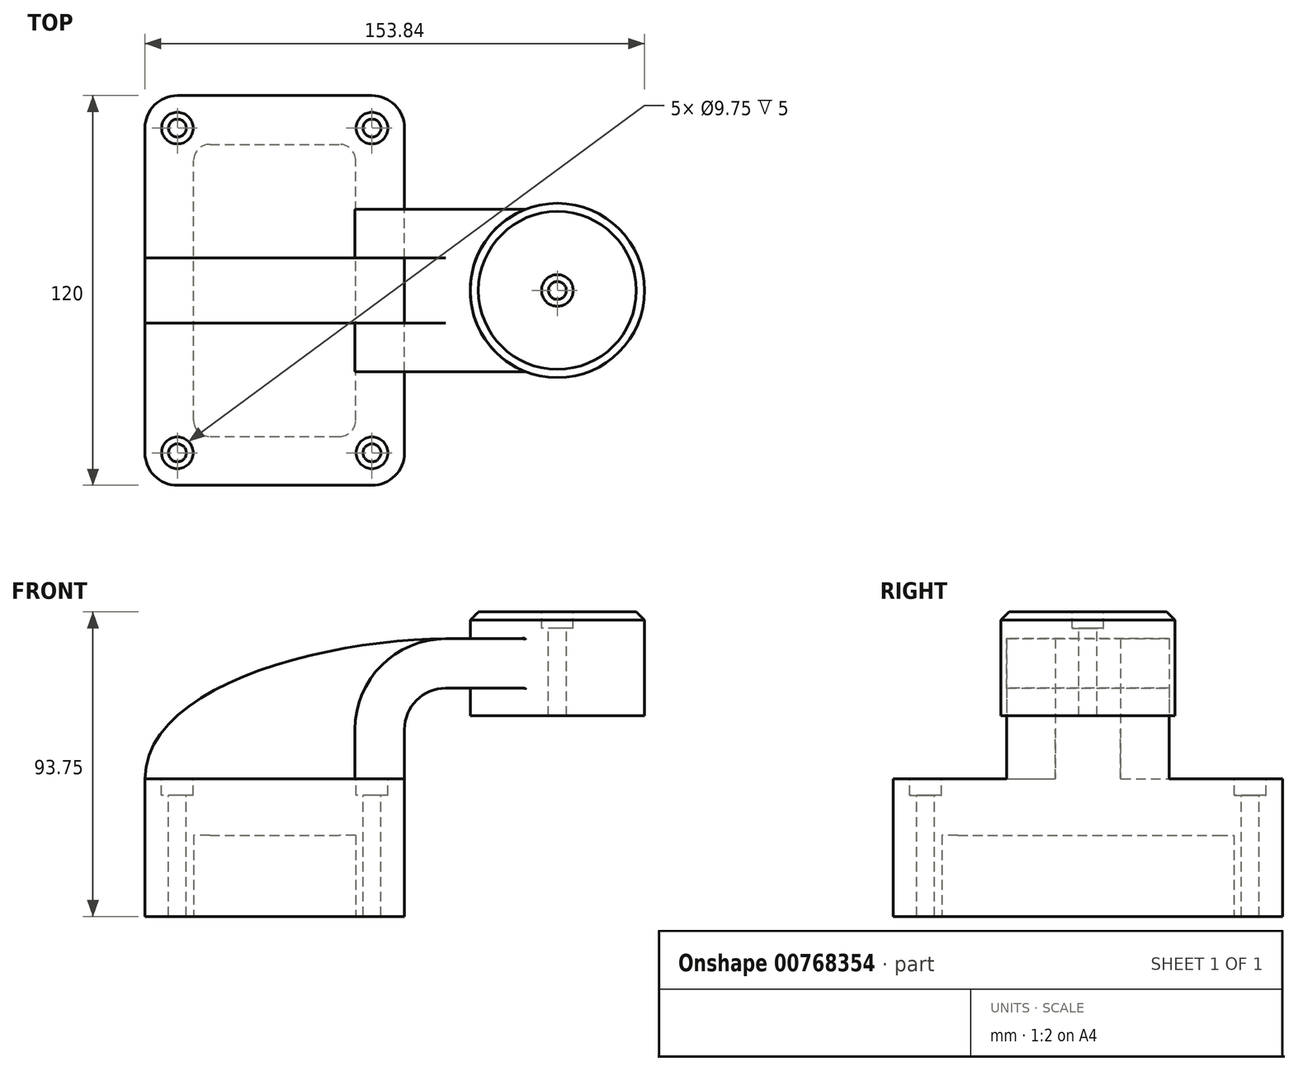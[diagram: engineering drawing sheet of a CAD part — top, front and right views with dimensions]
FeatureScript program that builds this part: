
annotation { "Feature Type Name" : "Feature", "Feature Type Description" : "" }
export const myFeature = defineFeature(function(context is Context, id is Id, definition is map)
    precondition{}
    {
        {
            assignVariable(context, id + "F0", {"name" : "chamferRadius", "anyValue" : 0.2});
        }
        {
            var Q0;
            Q0=qCreatedBy(makeId("Front.planeOp"),FACE);
            var sketch = newSketch(context, id + "F1", { "sketchPlane" : qUnion([Q0])});
            skLineSegment(sketch, "E0.bottom", {"start": v(39.95, -21.16) * mm, "end": v(-39.95, -21.16) * mm});
            skLineSegment(sketch, "E0.top", {"start": v(39.95, 21.16) * mm, "end": v(-39.95, 21.16) * mm});
            skLineSegment(sketch, "E0.left", {"start": v(39.95, -21.16) * mm, "end": v(39.95, 21.16) * mm});
            skLineSegment(sketch, "E0.right", {"start": v(-39.95, -21.16) * mm, "end": v(-39.95, 21.16) * mm});
            skPoint(sketch, "E0.middle", {"position": v(0, 0) * mm});
            skLineSegment(sketch, "E1.bottom", {"start": v(113.89, 40.6) * mm, "end": v(60.19, 40.6) * mm});
            skLineSegment(sketch, "E1.top", {"start": v(113.89, 72.6) * mm, "end": v(60.19, 72.6) * mm});
            skLineSegment(sketch, "E1.left", {"start": v(113.89, 40.6) * mm, "end": v(113.89, 72.6) * mm});
            skLineSegment(sketch, "E1.right", {"start": v(60.19, 40.6) * mm, "end": v(60.19, 72.6) * mm});
            skPoint(sketch, "E1.middle", {"position": v(87.04, 56.6) * mm});
            skLineSegment(sketch, "E2", {"start": v(39.95, 21.16) * mm, "end": v(39.95, 36.4) * mm});
            skArc(sketch, "E3", {"start": v(52.65, 49.1) * mm, "mid": v(43.67, 45.38) * mm, "end": v(39.95, 36.4) * mm});
            skLineSegment(sketch, "E4", {"start": v(52.65, 49.1) * mm, "end": v(87.04, 49.1) * mm});
            skLineSegment(sketch, "E5.0", {"start": v(24.71, 21.16) * mm, "end": v(24.71, 36.4) * mm});
            skArc(sketch, "E5.1", {"start": v(52.65, 64.34) * mm, "mid": v(32.9, 56.16) * mm, "end": v(24.71, 36.4) * mm});
            skLineSegment(sketch, "E5.2", {"start": v(52.65, 64.34) * mm, "end": v(87.04, 64.34) * mm});
            skLineSegment(sketch, "E6", {"start": v(87.04, 72.6) * mm, "end": v(87.04, 40.6) * mm});
            skFitSpline(sketch, "E7", {"points": [v(52.65, 64.34) * mm, v(-39.95, 21.16) * mm], "startDerivative": vector(-108.23, 0) * mm, "endDerivative": vector(0, -87.13) * mm});
            skSolve(sketch);
        }
        {
            var Q0;
            Q0=makeQuery(id+"F1.imprint","IMPRINT",FACE,{"disambiguationData":[TD([[makeQuery(id+"F1.imprint","IMPRINT",EDGE,{"derivedFrom":sQuery(id+"F1.wireOp",EDGE,"E0.bottom")}),-1.0]])]});
            extrude(context, id + "F2", {"entities" : qUnion([Q0]), "endBound" : BoundingType.SYMMETRIC, "depth" : 120 * mm, "offsetDistance" : 25.4 * mm});
        }
        {
            var Q0;
            {var subQ1=sQuery(id+"F1.wireOp",EDGE,"E2");Q0=makeQuery(id+"F1.imprint","IMPRINT",FACE,{"disambiguationData":[TD([[makeQuery(id+"F1.imprint","IMPRINT",EDGE,{"derivedFrom":subQ1}),1.0]])]});}
            var Q1;
            {var subQ0=sQuery(id+"F1.wireOp",EDGE,"E4");var subQ1=sQuery(id+"F1.wireOp",EDGE,"E1.right");var subQ2=makeQuery(id+"F1.imprint","INTERSECT",VERTEX,{"derivedFrom":[subQ1,subQ0]});Q1=makeQuery(id+"F1.imprint","IMPRINT",FACE,{"disambiguationData":[TD([[makeQuery(id+"F1.imprint","IMPRINT",EDGE,{"disambiguationData":[TD([[subQ2,-1.0]])],"derivedFrom":subQ1}),-1.0]])]});}
            extrude(context, id + "F3", {"entities" : qUnion([Q0, Q1]), "operationType" : NewBodyOperationType.ADD, "endBound" : BoundingType.SYMMETRIC, "depth" : 50 * mm, "offsetDistance" : 25.4 * mm});
        }
        {
            var Q0;
            {var subQ2=sQuery(id+"F1.wireOp",EDGE,"E5.0");Q0=makeQuery(id+"F1.imprint","IMPRINT",FACE,{"disambiguationData":[TD([[makeQuery(id+"F1.imprint","IMPRINT",EDGE,{"derivedFrom":subQ2}),1.0]])]});}
            extrude(context, id + "F4", {"entities" : qUnion([Q0]), "operationType" : NewBodyOperationType.ADD, "endBound" : BoundingType.SYMMETRIC, "depth" : 20 * mm, "offsetDistance" : 25.4 * mm});
        }
        {
            var Q0;
            {var subQ4=sQuery(id+"F1.wireOp",EDGE,"E1.left");Q0=makeQuery(id+"F1.imprint","IMPRINT",FACE,{"disambiguationData":[TD([[makeQuery(id+"F1.imprint","IMPRINT",EDGE,{"derivedFrom":subQ4}),1.0]])]});}
            var Q1;
            Q1=sQuery(id+"F1.wireOp",EDGE,"E6");
            revolve(context, id + "F5", {"operationType" : NewBodyOperationType.ADD, "surfaceOperationType" : NewSurfaceOperationType.NEW, "entities" : qUnion([Q0]), "axis" : qUnion([Q1]), "revolveType" : RevolveType.FULL});
        }
        {
            var Q0;
            Q0=makeQuery(id+"F2.opExtrude","CAP_EDGE",EDGE,{"disambiguationData":[OSD([sQuery(id+"F1.wireOp",EDGE,"E0.left")])],"isStart":false});
            var Q1;
            Q1=makeQuery(id+"F2.opExtrude","CAP_EDGE",EDGE,{"disambiguationData":[OSD([sQuery(id+"F1.wireOp",EDGE,"E0.right")])],"isStart":false});
            var Q2;
            Q2=makeQuery(id+"F2.opExtrude","CAP_EDGE",EDGE,{"disambiguationData":[OSD([sQuery(id+"F1.wireOp",EDGE,"E0.left")])],"isStart":true});
            var Q3;
            Q3=makeQuery(id+"F2.opExtrude","CAP_EDGE",EDGE,{"disambiguationData":[OSD([sQuery(id+"F1.wireOp",EDGE,"E0.right")])],"isStart":true});
            fillet(context, id + "F6", {"entities" : qUnion([Q0, Q1, Q2, Q3]), "radius" : 10 * mm, "tangentPropagation" : true, "allowEdgeOverflow" : false});
        }
        {
            var Q0;
            Q0=makeQuery(id+"F5.boolean.opBoolean","INTERSECT",EDGE,{"derivedFrom":[makeQuery(id+"F3.opExtrude","CAP_FACE",FACE,{"disambiguationData":[OSD([sQuery(id+"F1.wireOp",EDGE,"E0.top"),sQuery(id+"F1.wireOp",EDGE,"E2"),sQuery(id+"F1.wireOp",EDGE,"E3"),sQuery(id+"F1.wireOp",EDGE,"E4"),sQuery(id+"F1.wireOp",EDGE,"E5.0"),sQuery(id+"F1.wireOp",EDGE,"E5.1"),sQuery(id+"F1.wireOp",EDGE,"E5.2"),sQuery(id+"F1.wireOp",EDGE,"E6")])],"isStart":true}),makeQuery(id+"F5.opRevolve","SWEPT_FACE",FACE,{"disambiguationData":[OSD([sQuery(id+"F1.wireOp",EDGE,"E1.left")])]})]});
            var Q1;
            Q1=makeQuery(id+"F5.boolean.opBoolean","INTERSECT",EDGE,{"derivedFrom":[makeQuery(id+"F3.opExtrude","SWEPT_FACE",FACE,{"disambiguationData":[OSD([sQuery(id+"F1.wireOp",EDGE,"E5.2")])]}),makeQuery(id+"F5.opRevolve","SWEPT_FACE",FACE,{"disambiguationData":[OSD([sQuery(id+"F1.wireOp",EDGE,"E1.left")])]})]});
            var Q2;
            Q2=makeQuery(id+"F5.boolean.opBoolean","INTERSECT",EDGE,{"derivedFrom":[makeQuery(id+"F3.opExtrude","CAP_FACE",FACE,{"disambiguationData":[OSD([sQuery(id+"F1.wireOp",EDGE,"E0.top"),sQuery(id+"F1.wireOp",EDGE,"E2"),sQuery(id+"F1.wireOp",EDGE,"E3"),sQuery(id+"F1.wireOp",EDGE,"E4"),sQuery(id+"F1.wireOp",EDGE,"E5.0"),sQuery(id+"F1.wireOp",EDGE,"E5.1"),sQuery(id+"F1.wireOp",EDGE,"E5.2"),sQuery(id+"F1.wireOp",EDGE,"E6")])],"isStart":false}),makeQuery(id+"F5.opRevolve","SWEPT_FACE",FACE,{"disambiguationData":[OSD([sQuery(id+"F1.wireOp",EDGE,"E1.left")])]})]});
            var Q3;
            Q3=makeQuery(id+"F5.boolean.opBoolean","INTERSECT",EDGE,{"derivedFrom":[makeQuery(id+"F3.opExtrude","SWEPT_FACE",FACE,{"disambiguationData":[OSD([sQuery(id+"F1.wireOp",EDGE,"E4")])]}),makeQuery(id+"F5.opRevolve","SWEPT_FACE",FACE,{"disambiguationData":[OSD([sQuery(id+"F1.wireOp",EDGE,"E1.left")])]})]});
            var Q4;
            Q4=makeQuery(id+"F3.opExtrude","CAP_EDGE",EDGE,{"disambiguationData":[OSD([sQuery(id+"F1.wireOp",EDGE,"E5.2")])],"isStart":false});
            var Q5;
            Q5=makeQuery(id+"F3.opExtrude","CAP_EDGE",EDGE,{"disambiguationData":[OSD([sQuery(id+"F1.wireOp",EDGE,"E5.2")])],"isStart":true});
            var Q6;
            Q6=makeQuery(id+"F3.opExtrude","CAP_EDGE",EDGE,{"disambiguationData":[OSD([sQuery(id+"F1.wireOp",EDGE,"E5.1")])],"isStart":false});
            var Q7;
            Q7=makeQuery(id+"F3.opExtrude","CAP_EDGE",EDGE,{"disambiguationData":[OSD([sQuery(id+"F1.wireOp",EDGE,"E5.0")])],"isStart":false});
            var Q8;
            Q8=makeQuery(id+"F3.opExtrude","CAP_EDGE",EDGE,{"disambiguationData":[OSD([sQuery(id+"F1.wireOp",EDGE,"E5.1")])],"isStart":true});
            var Q9;
            Q9=makeQuery(id+"F3.opExtrude","CAP_EDGE",EDGE,{"disambiguationData":[OSD([sQuery(id+"F1.wireOp",EDGE,"E5.0")])],"isStart":true});
            var Q10;
            Q10=makeQuery(id+"F3.opExtrude","CAP_EDGE",EDGE,{"disambiguationData":[OSD([sQuery(id+"F1.wireOp",EDGE,"E0.top")])],"isStart":true});
            var Q11;
            {var subQ0=sQuery(id+"F1.wireOp",EDGE,"E0.top");var subQ1=sQuery(id+"F1.wireOp",EDGE,"E5.1");var subQ2=sQuery(id+"F1.wireOp",EDGE,"E5.0");Q11=makeQuery(id+"F4.boolean.opBoolean","SPLIT",EDGE,{"disambiguationData":[TD([makeQuery(id+"F4.opExtrude","CAP_FACE",FACE,{"disambiguationData":[OSD([subQ0,subQ2,subQ1,sQuery(id+"F1.wireOp",EDGE,"E7")])],"isStart":true})])],"derivedFrom":makeQuery(id+"F3.opExtrude","SWEPT_EDGE",EDGE,{"disambiguationData":[OSD([subQ0,subQ2])]})});}
            var Q12;
            {var subQ0=sQuery(id+"F1.wireOp",EDGE,"E0.top");var subQ1=sQuery(id+"F1.wireOp",EDGE,"E5.1");var subQ2=sQuery(id+"F1.wireOp",EDGE,"E5.0");Q12=makeQuery(id+"F4.boolean.opBoolean","SPLIT",EDGE,{"disambiguationData":[TD([makeQuery(id+"F4.opExtrude","CAP_FACE",FACE,{"disambiguationData":[OSD([subQ0,subQ2,subQ1,sQuery(id+"F1.wireOp",EDGE,"E7")])],"isStart":false})])],"derivedFrom":makeQuery(id+"F3.opExtrude","SWEPT_EDGE",EDGE,{"disambiguationData":[OSD([subQ0,subQ2])]})});}
            var Q13;
            Q13=makeQuery(id+"F3.opExtrude","CAP_EDGE",EDGE,{"disambiguationData":[OSD([sQuery(id+"F1.wireOp",EDGE,"E0.top")])],"isStart":false});
            var Q14;
            Q14=makeQuery(id+"F4.opExtrude","CAP_EDGE",EDGE,{"disambiguationData":[OSD([sQuery(id+"F1.wireOp",EDGE,"E0.top")])],"isStart":true});
            var Q15;
            Q15=makeQuery(id+"F4.opExtrude","CAP_EDGE",EDGE,{"disambiguationData":[OSD([sQuery(id+"F1.wireOp",EDGE,"E0.top")])],"isStart":false});
            fillet(context, id + "F7", {"entities" : qUnion([Q0, Q1, Q2, Q3, Q4, Q5, Q6, Q7, Q8, Q9, Q10, Q11, Q12, Q13, Q14, Q15]), "radius" : (getVariable(context, 'chamferRadius')) * mm, "tangentPropagation" : true, "allowEdgeOverflow" : false});
        }
        {
            var Q0;
            Q0=makeQuery(id+"F5.opRevolve","SWEPT_FACE",FACE,{"disambiguationData":[OSD([sQuery(id+"F1.wireOp",EDGE,"E1.top")])]});
            var sketch = newSketch(context, id + "F8", { "sketchPlane" : qUnion([Q0])});
            skPoint(sketch, "E8", {"position": v(87.04, 0) * mm});
            skSolve(sketch);
        }
        {
            var Q0;
            Q0=sQuery(id+"F8.wireOp",VERTEX,"E8");
            var Q1;
            Q1=makeQuery(id+"F2.opExtrude","SWEPT_BODY",BODY,{"disambiguationData":[OSD([sQuery(id+"F1.wireOp",EDGE,"E0.bottom"),sQuery(id+"F1.wireOp",EDGE,"E0.top"),sQuery(id+"F1.wireOp",EDGE,"E0.left"),sQuery(id+"F1.wireOp",EDGE,"E0.right")])]});
            hole(context, id + "F9", {"style" : HoleStyle.C_BORE, "endStyle" : HoleEndStyle.THROUGH, "standardTappedOrClearance" : lookupTablePath({ "standard" : "ISO", "fit" : "Normal", "engagement" : "75%", "pitch" : "0.8 mm", "size" : "M5", "type" : "Clearance" }), "standardBlindInLast" : lookupTablePath({ "fit" : "Standard", "standard" : "ISO", "engagement" : "75%", "pitch" : "0.8 mm", "size" : "M5", "type" : "Clearance" }), "holeDiameter" : 5.5 * mm, "cBoreDiameter" : 9.75 * mm, "cBoreDepth" : 5 * mm, "majorDiameter" : 5 * mm, "showTappedDepth" : true, "isTappedThrough" : true, "tappedDepth" : 3.95 * mm, "tapClearance" : 3, "locations" : qUnion([Q0]), "scope" : qUnion([Q1])});
        }
        {
            var Q0;
            Q0=makeQuery(id+"F5.opRevolve","SWEPT_EDGE",EDGE,{"disambiguationData":[OSD([sQuery(id+"F1.wireOp",EDGE,"E1.top"),sQuery(id+"F1.wireOp",EDGE,"E1.left")])]});
            chamfer(context, id + "F10", {"entities" : qUnion([Q0]), "width" : 2.54 * mm, "tangentPropagation" : true});
        }
        {
            var Q0;
            {var subQ3=sQuery(id+"F1.wireOp",EDGE,"E0.top");var subQ4=sQuery(id+"F1.wireOp",EDGE,"E0.right");var subQ5=sQuery(id+"F1.wireOp",EDGE,"E0.left");Q0=makeQuery(id+"F4.boolean.opBoolean","SPLIT",FACE,{"disambiguationData":[TD([makeQuery(id+"F2.opExtrude","CAP_FACE",FACE,{"disambiguationData":[OSD([sQuery(id+"F1.wireOp",EDGE,"E0.bottom"),subQ3,subQ5,subQ4])],"isStart":true})])],"derivedFrom":makeQuery(id+"F2.opExtrude","SWEPT_FACE",FACE,{"disambiguationData":[OSD([subQ3])]})});}
            var sketch = newSketch(context, id + "F11", { "sketchPlane" : qUnion([Q0])});
            skPoint(sketch, "E9", {"position": v(29.95, 50) * mm});
            skPoint(sketch, "E10", {"position": v(-29.95, 50) * mm});
            skSolve(sketch);
        }
        {
            var Q0;
            {var subQ3=sQuery(id+"F1.wireOp",EDGE,"E0.top");var subQ5=sQuery(id+"F1.wireOp",EDGE,"E0.right");var subQ6=sQuery(id+"F1.wireOp",EDGE,"E0.left");Q0=makeQuery(id+"F4.boolean.opBoolean","SPLIT",FACE,{"disambiguationData":[TD([makeQuery(id+"F2.opExtrude","CAP_FACE",FACE,{"disambiguationData":[OSD([sQuery(id+"F1.wireOp",EDGE,"E0.bottom"),subQ3,subQ6,subQ5])],"isStart":false})])],"derivedFrom":makeQuery(id+"F2.opExtrude","SWEPT_FACE",FACE,{"disambiguationData":[OSD([subQ3])]})});}
            var sketch = newSketch(context, id + "F12", { "sketchPlane" : qUnion([Q0])});
            skPoint(sketch, "E11", {"position": v(29.95, -50) * mm});
            skPoint(sketch, "E12", {"position": v(-29.95, -50) * mm});
            skSolve(sketch);
        }
        {
            var Q0;
            Q0=sQuery(id+"F11.wireOp",VERTEX,"E10");
            var Q1;
            Q1=sQuery(id+"F11.wireOp",VERTEX,"E9");
            var Q2;
            Q2=sQuery(id+"F12.wireOp",VERTEX,"E11");
            var Q3;
            Q3=sQuery(id+"F12.wireOp",VERTEX,"E12");
            var Q4;
            Q4=makeQuery(id+"F2.opExtrude","SWEPT_BODY",BODY,{"disambiguationData":[OSD([sQuery(id+"F1.wireOp",EDGE,"E0.bottom"),sQuery(id+"F1.wireOp",EDGE,"E0.top"),sQuery(id+"F1.wireOp",EDGE,"E0.left"),sQuery(id+"F1.wireOp",EDGE,"E0.right")])]});
            hole(context, id + "F13", {"style" : HoleStyle.C_BORE, "endStyle" : HoleEndStyle.THROUGH, "standardTappedOrClearance" : lookupTablePath({ "standard" : "ISO", "fit" : "Normal", "size" : "M5", "type" : "Clearance" }), "standardBlindInLast" : lookupTablePath({ "fit" : "Standard", "standard" : "ISO", "size" : "M5", "type" : "Clearance" }), "holeDiameter" : 5.5 * mm, "cBoreDiameter" : 9.75 * mm, "cBoreDepth" : 5 * mm, "majorDiameter" : 5 * mm, "isTappedThrough" : true, "tappedDepth" : 12 * mm, "tapClearance" : 3, "locations" : qUnion([Q0, Q1, Q2, Q3]), "scope" : qUnion([Q4])});
        }
        {
            var Q0;
            Q0=makeQuery(id+"F2.opExtrude","SWEPT_FACE",FACE,{"disambiguationData":[OSD([sQuery(id+"F1.wireOp",EDGE,"E0.bottom")])]});
            var sketch = newSketch(context, id + "F14", { "sketchPlane" : qUnion([Q0])});
            skLineSegment(sketch, "E13.bottom", {"start": v(-29.95, 50) * mm, "end": v(29.95, 50) * mm});
            skLineSegment(sketch, "E13.top", {"start": v(-29.95, -50) * mm, "end": v(29.95, -50) * mm});
            skLineSegment(sketch, "E13.left", {"start": v(-29.95, 50) * mm, "end": v(-29.95, -50) * mm});
            skLineSegment(sketch, "E13.right", {"start": v(29.95, 50) * mm, "end": v(29.95, -50) * mm});
            skLineSegment(sketch, "E14.0", {"start": v(-24.95, 40) * mm, "end": v(-24.95, -40) * mm});
            skLineSegment(sketch, "E14.1", {"start": v(-19.95, 45) * mm, "end": v(19.95, 45) * mm});
            skLineSegment(sketch, "E14.2", {"start": v(24.95, 40) * mm, "end": v(24.95, -40) * mm});
            skLineSegment(sketch, "E14.3", {"start": v(-19.95, -45) * mm, "end": v(19.95, -45) * mm});
            skPoint(sketch, "E15.visualSharp", {"position": v(-24.95, 45) * mm});
            skArc(sketch, "E15.filletArc", {"start": v(-19.95, 45) * mm, "mid": v(-23.49, 43.54) * mm, "end": v(-24.95, 40) * mm});
            skPoint(sketch, "E16.visualSharp", {"position": v(24.95, 45) * mm});
            skArc(sketch, "E16.filletArc", {"start": v(24.95, 40) * mm, "mid": v(23.49, 43.54) * mm, "end": v(19.95, 45) * mm});
            skPoint(sketch, "E17.visualSharp", {"position": v(24.95, -45) * mm});
            skArc(sketch, "E17.filletArc", {"start": v(19.95, -45) * mm, "mid": v(23.49, -43.54) * mm, "end": v(24.95, -40) * mm});
            skPoint(sketch, "E18.visualSharp", {"position": v(-24.95, -45) * mm});
            skArc(sketch, "E18.filletArc", {"start": v(-24.95, -40) * mm, "mid": v(-23.49, -43.54) * mm, "end": v(-19.95, -45) * mm});
            skSolve(sketch);
        }
        {
            var Q0;
            Q0=makeQuery(id+"F14.imprint","IMPRINT",FACE,{"disambiguationData":[TD([[makeQuery(id+"F14.imprint","IMPRINT",EDGE,{"derivedFrom":sQuery(id+"F14.wireOp",EDGE,"E14.0")}),1.0]])]});
            extrude(context, id + "F15", {"entities" : qUnion([Q0]), "operationType" : NewBodyOperationType.REMOVE, "oppositeDirection" : true, "depth" : 25 * mm, "offsetDistance" : 25 * mm});
        }
    });
